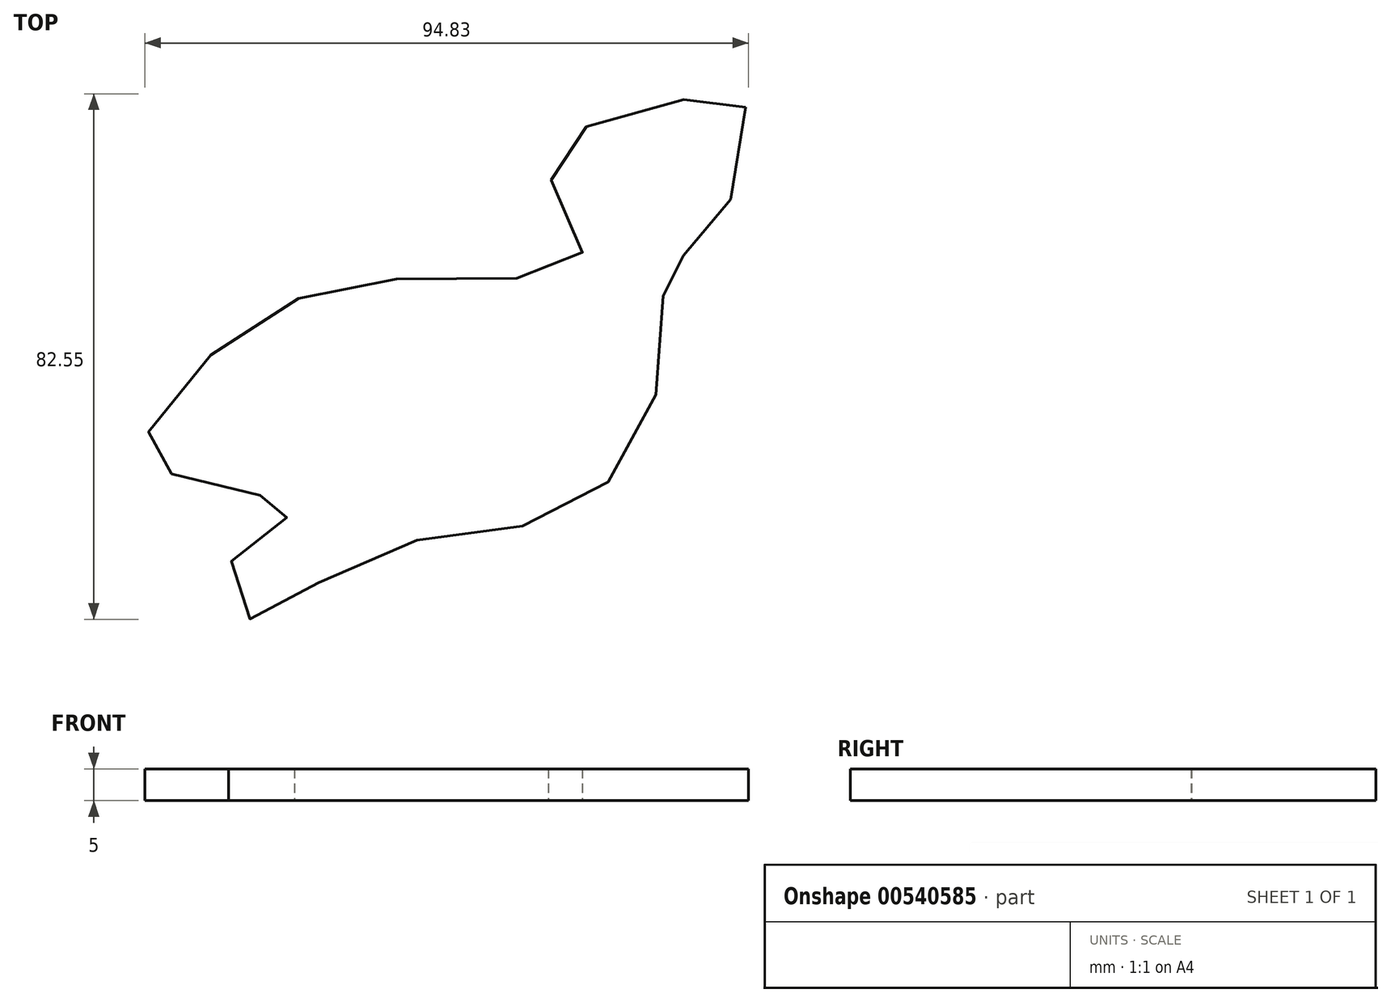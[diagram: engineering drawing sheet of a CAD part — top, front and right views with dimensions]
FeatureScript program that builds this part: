
annotation { "Feature Type Name" : "Feature", "Feature Type Description" : "" }
export const myFeature = defineFeature(function(context is Context, id is Id, definition is map)
    precondition{}
    {
        {
            var Q0;
            Q0=qCreatedBy(makeId("Top.planeOp"),FACE);
            var sketch = newSketch(context, id + "F0", { "sketchPlane" : qUnion([Q0])});
            skFitSpline(sketch, "E0", {"points": [v(25.74, 74.24) * mm, v(18.65, 52.23) * mm, v(13.8, 49.99) * mm, v(11.94, 30.59) * mm, v(-3.73, 10.07) * mm, v(-34.32, 3.73) * mm, v(-52.6, -5.97) * mm, v(-54.1, 4.85) * mm, v(-45.14, 10.82) * mm, v(-59.31, 15.3) * mm, v(-68.64, 20.52) * mm, v(-52.97, 39.54) * mm, v(-25.74, 47.38) * mm, v(0, 50.73) * mm, v(-5.22, 65.66) * mm, v(12.68, 74.6) * mm, v(25.74, 74.24) * mm]});
            skSolve(sketch);
        }
        {
            var Q0;
            Q0 = qSketchRegion(id + "F0", true);
            extrude(context, id + "F1", {"entities" : qUnion([Q0]), "depth" : 5 * mm, "offsetDistance" : 25 * mm});
        }
    });
